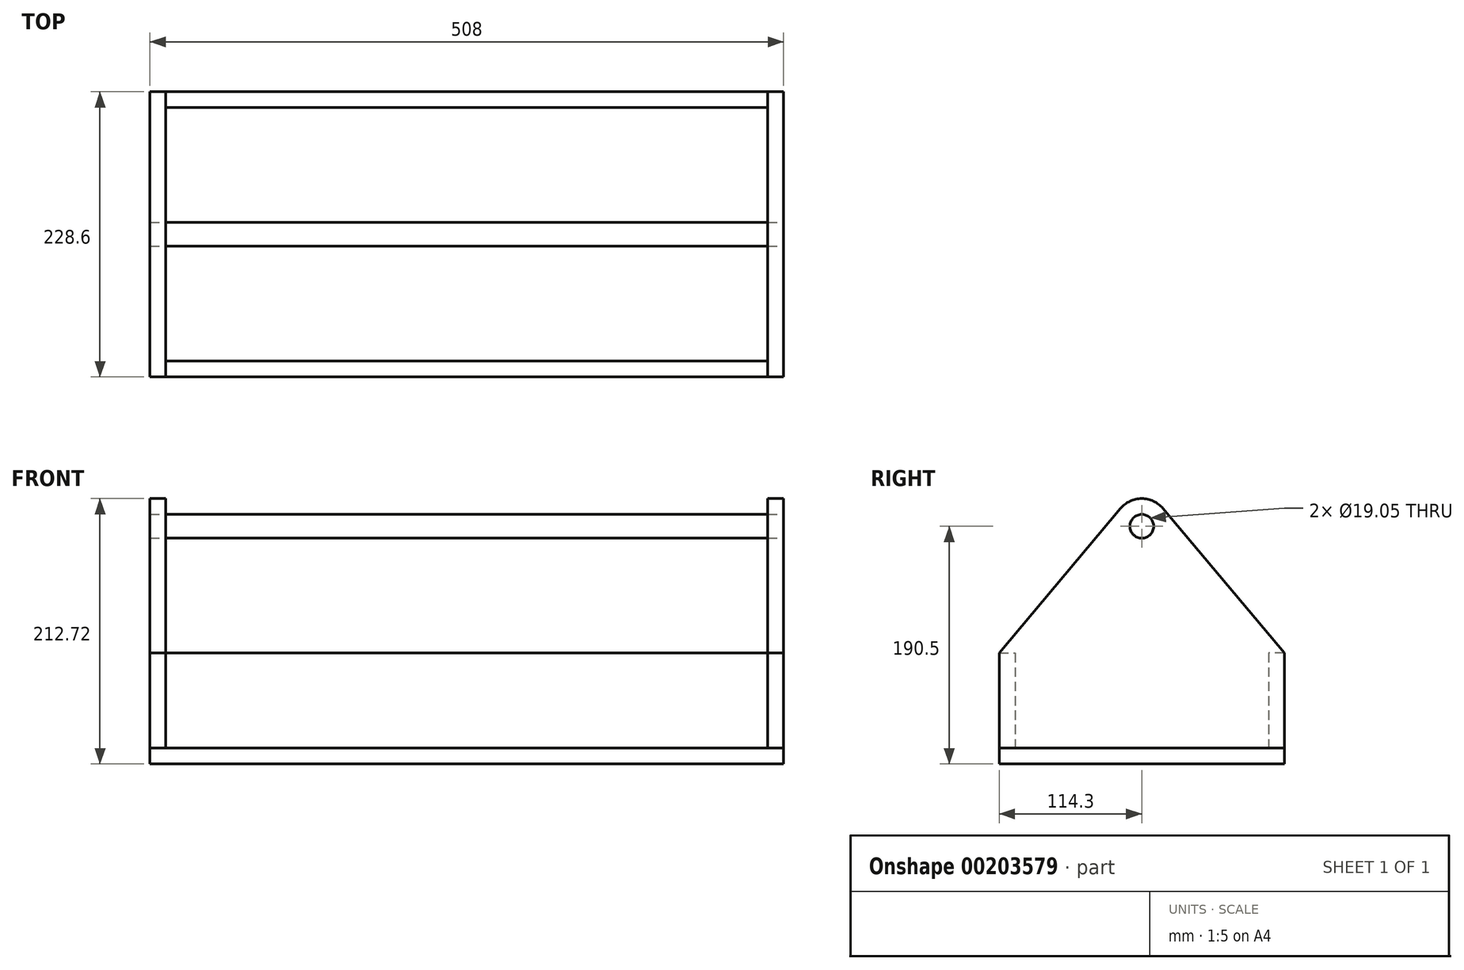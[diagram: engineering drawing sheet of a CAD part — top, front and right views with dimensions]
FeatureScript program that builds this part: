
annotation { "Feature Type Name" : "Feature", "Feature Type Description" : "" }
export const myFeature = defineFeature(function(context is Context, id is Id, definition is map)
    precondition{}
    {
        {
            var Q0;
            Q0=qCreatedBy(makeId("Top.planeOp"),FACE);
            var sketch = newSketch(context, id + "F0", { "sketchPlane" : qUnion([Q0])});
            skLineSegment(sketch, "E0.bottom", {"start": v(-254, 114.3) * mm, "end": v(254, 114.3) * mm});
            skLineSegment(sketch, "E0.top", {"start": v(-254, -114.3) * mm, "end": v(254, -114.3) * mm});
            skLineSegment(sketch, "E0.left", {"start": v(-254, 114.3) * mm, "end": v(-254, -114.3) * mm});
            skLineSegment(sketch, "E0.right", {"start": v(254, 114.3) * mm, "end": v(254, -114.3) * mm});
            skPoint(sketch, "E0.middle", {"position": v(0, 0) * mm});
            skSolve(sketch);
        }
        {
            var Q0;
            Q0=makeQuery(id+"F0.imprint","IMPRINT",FACE,{"disambiguationData":[TD([[makeQuery(id+"F0.imprint","IMPRINT",EDGE,{"derivedFrom":sQuery(id+"F0.wireOp",EDGE,"E0.bottom")}),-1.0]])]});
            extrude(context, id + "F1", {"entities" : qUnion([Q0]), "depth" : 12.7 * mm});
        }
        {
            var Q0;
            Q0=makeQuery(id+"F1.opExtrude","SWEPT_FACE",FACE,{"disambiguationData":[OSD([sQuery(id+"F0.wireOp",EDGE,"E0.right")])]});
            var sketch = newSketch(context, id + "F2", { "sketchPlane" : qUnion([Q0])});
            skLineSegment(sketch, "E1", {"start": v(-114.3, 12.7) * mm, "end": v(-114.3, 88.9) * mm});
            skLineSegment(sketch, "E2", {"start": v(114.3, 12.7) * mm, "end": v(114.3, 88.9) * mm});
            skCircle(sketch, "E3", {"center": v(0, 190.5) * mm, "radius": 9.53 * mm});
            skPoint(sketch, "E3.centerSnap0", {"position": v(0, 12.7) * mm});
            skArc(sketch, "E4.0", {"start": v(17.02, 204.79) * mm, "mid": v(0, 212.72) * mm, "end": v(-17.02, 204.79) * mm});
            skLineSegment(sketch, "E5", {"start": v(-114.3, 88.9) * mm, "end": v(-17.02, 204.79) * mm});
            skLineSegment(sketch, "E6", {"start": v(114.3, 88.9) * mm, "end": v(17.02, 204.79) * mm});
            skSolve(sketch);
        }
        {
            var Q0;
            Q0=makeQuery(id+"F2.imprint","IMPRINT",FACE,{"disambiguationData":[TD([[makeQuery(id+"F2.imprint","IMPRINT",EDGE,{"derivedFrom":sQuery(id+"F2.wireOp",EDGE,"E1")}),-1.0]])]});
            extrude(context, id + "F3", {"entities" : qUnion([Q0]), "oppositeDirection" : true, "depth" : 12.7 * mm});
        }
        {
            var Q0;
            Q0=makeQuery(id+"F3.opExtrude","SWEPT_BODY",BODY,{"disambiguationData":[OSD([sQuery(id+"F0.wireOp",EDGE,"E0.right"),sQuery(id+"F2.wireOp",EDGE,"E1"),sQuery(id+"F2.wireOp",EDGE,"E2"),sQuery(id+"F2.wireOp",EDGE,"E3"),sQuery(id+"F2.wireOp",EDGE,"E4.0"),sQuery(id+"F2.wireOp",EDGE,"E5"),sQuery(id+"F2.wireOp",EDGE,"E6")])]});
            var Q1;
            Q1=qCreatedBy(makeId("Right.planeOp"),FACE);
            mirror(context, id + "F4", {"entities" : qUnion([Q0]), "mirrorPlane" : qUnion([Q1])});
        }
        {
            var Q0;
            Q0=makeQuery(id+"F1.opExtrude","CAP_FACE",FACE,{"disambiguationData":[OSD([sQuery(id+"F0.wireOp",EDGE,"E0.bottom"),sQuery(id+"F0.wireOp",EDGE,"E0.top"),sQuery(id+"F0.wireOp",EDGE,"E0.left"),sQuery(id+"F0.wireOp",EDGE,"E0.right")])],"isStart":false});
            var sketch = newSketch(context, id + "F5", { "sketchPlane" : qUnion([Q0])});
            skLineSegment(sketch, "E7.0", {"start": v(241.3, 114.3) * mm, "end": v(241.3, -114.3) * mm});
            skLineSegment(sketch, "E8.0", {"start": v(-254, 114.3) * mm, "end": v(254, 114.3) * mm});
            skLineSegment(sketch, "E9.0", {"start": v(-241.3, 114.3) * mm, "end": v(-241.3, -114.3) * mm});
            skLineSegment(sketch, "E10", {"start": v(241.3, 101.6) * mm, "end": v(-241.3, 101.6) * mm});
            skSolve(sketch);
        }
        {
            var Q0;
            {var subQ3=sQuery(id+"F5.wireOp",EDGE,"E10");Q0=makeQuery(id+"F5.imprint","IMPRINT",FACE,{"disambiguationData":[TD([[makeQuery(id+"F5.imprint","IMPRINT",EDGE,{"derivedFrom":subQ3}),-1.0]])]});}
            var Q1;
            Q1=makeQuery(id+"F4.opPattern","COPY",VERTEX,{"derivedFrom":makeQuery(id+"F3.opExtrude","CAP_VERTEX",VERTEX,{"disambiguationData":[OSD([sQuery(id+"F2.wireOp",EDGE,"E2"),sQuery(id+"F2.wireOp",EDGE,"E6")])],"isStart":true}),"instanceName":"1"});
            extrude(context, id + "F6", {"entities" : qUnion([Q0]), "endBound" : BoundingType.UP_TO_VERTEX, "endBoundEntityVertex" : qUnion([Q1]), "depth" : 25.4 * mm});
        }
        {
            var Q0;
            Q0=makeQuery(id+"F6.opExtrude","SWEPT_BODY",BODY,{"disambiguationData":[OSD([sQuery(id+"F5.wireOp",EDGE,"E7.0"),sQuery(id+"F5.wireOp",EDGE,"E8.0"),sQuery(id+"F5.wireOp",EDGE,"E9.0"),sQuery(id+"F5.wireOp",EDGE,"E10")])]});
            var Q1;
            Q1=qCreatedBy(makeId("Front.planeOp"),FACE);
            mirror(context, id + "F7", {"entities" : qUnion([Q0]), "mirrorPlane" : qUnion([Q1])});
        }
        {
            var Q0;
            Q0=makeQuery(id+"F2.imprint","IMPRINT",FACE,{"disambiguationData":[TD([[makeQuery(id+"F2.imprint","IMPRINT",EDGE,{"derivedFrom":sQuery(id+"F2.wireOp",EDGE,"E3")}),1.0]])]});
            var Q1;
            Q1=makeQuery(id+"F4.opPattern","COPY",FACE,{"derivedFrom":makeQuery(id+"F3.opExtrude","CAP_FACE",FACE,{"disambiguationData":[OSD([sQuery(id+"F0.wireOp",EDGE,"E0.right"),sQuery(id+"F2.wireOp",EDGE,"E1"),sQuery(id+"F2.wireOp",EDGE,"E2"),sQuery(id+"F2.wireOp",EDGE,"E3"),sQuery(id+"F2.wireOp",EDGE,"E4.0"),sQuery(id+"F2.wireOp",EDGE,"E5"),sQuery(id+"F2.wireOp",EDGE,"E6")])],"isStart":true}),"instanceName":"1"});
            extrude(context, id + "F8", {"entities" : qUnion([Q0]), "endBound" : BoundingType.UP_TO_SURFACE, "oppositeDirection" : true, "endBoundEntityFace" : qUnion([Q1]), "depth" : 25.4 * mm});
        }
    });
